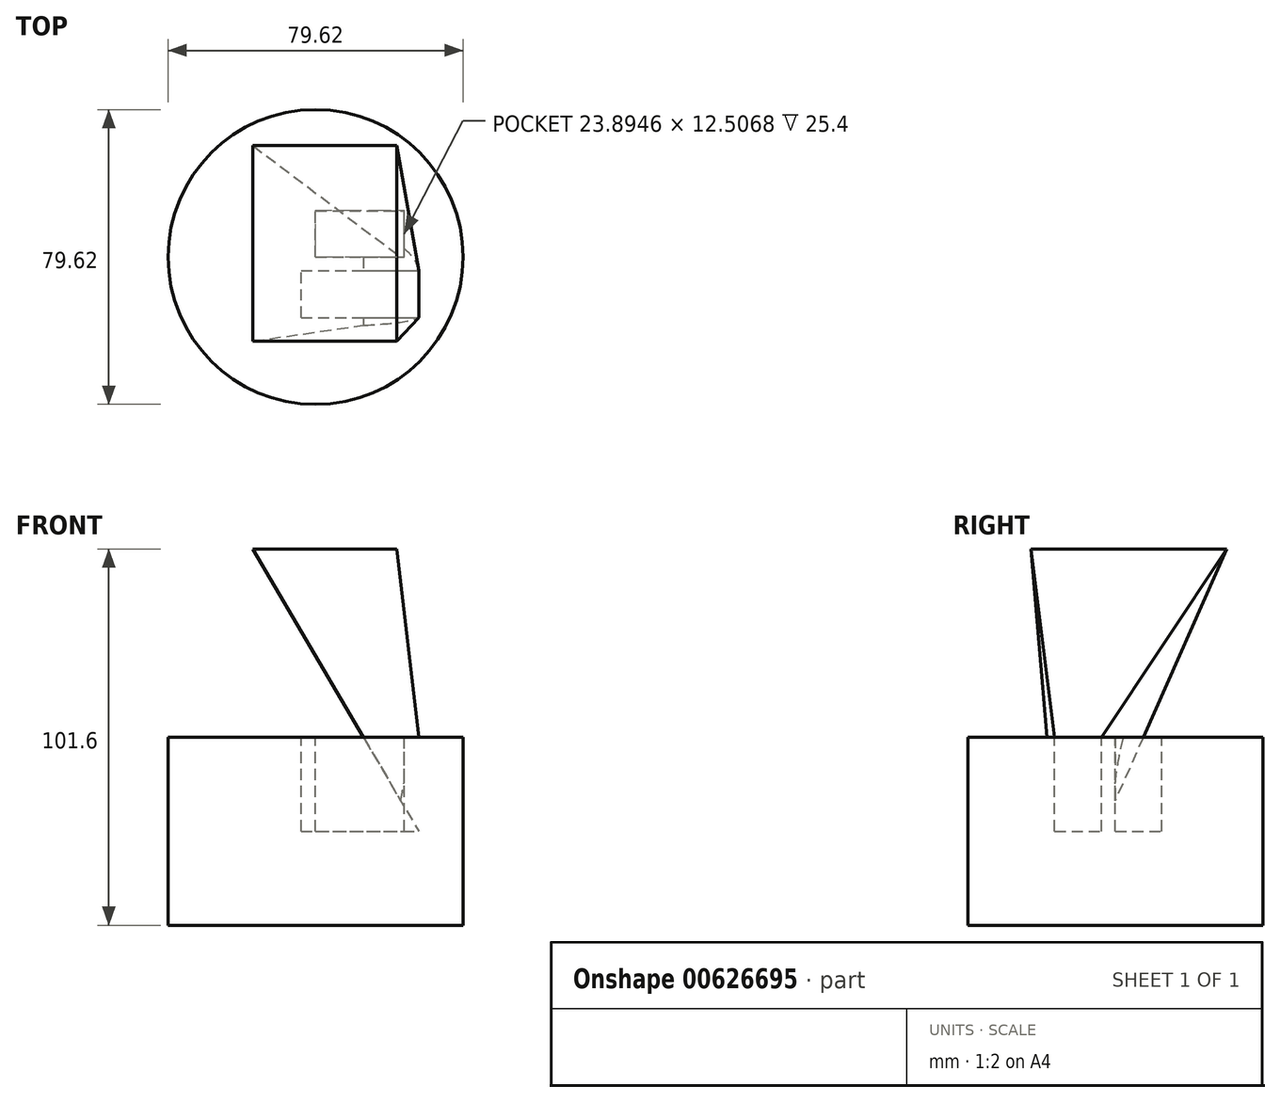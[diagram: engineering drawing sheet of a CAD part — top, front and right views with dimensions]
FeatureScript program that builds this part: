
annotation { "Feature Type Name" : "Feature", "Feature Type Description" : "" }
export const myFeature = defineFeature(function(context is Context, id is Id, definition is map)
    precondition{}
    {
        {
            var Q0;
            Q0=qCreatedBy(makeId("Top.planeOp"),FACE);
            var sketch = newSketch(context, id + "F0", { "sketchPlane" : qUnion([Q0])});
            skCircle(sketch, "E0", {"center": v(-11.95, 0) * mm, "radius": 39.8 * mm});
            skSolve(sketch);
        }
        {
            var Q0;
            Q0=makeQuery(id+"F0.imprint","IMPRINT",FACE,{"disambiguationData":[TD([[makeQuery(id+"F0.imprint","IMPRINT",EDGE,{"derivedFrom":sQuery(id+"F0.wireOp",EDGE,"E0")}),1.0]])]});
            extrude(context, id + "F1", {"entities" : qUnion([Q0]), "depth" : 25.4 * mm, "offsetDistance" : 25.4 * mm, "hasSecondDirection" : true, "secondDirectionOppositeDirection" : true, "secondDirectionDepth" : 25.4 * mm});
        }
        {
            var Q0;
            Q0=makeQuery(id+"F1.opExtrude","CAP_FACE",FACE,{"disambiguationData":[OSD([sQuery(id+"F0.wireOp",EDGE,"E0")])],"isStart":false});
            var sketch = newSketch(context, id + "F2", { "sketchPlane" : qUnion([Q0])});
            skLineSegment(sketch, "E1.bottom", {"start": v(-11.95, 0) * mm, "end": v(11.95, 0) * mm});
            skLineSegment(sketch, "E1.top", {"start": v(-11.95, 12.5) * mm, "end": v(11.95, 12.5) * mm});
            skLineSegment(sketch, "E1.left", {"start": v(-11.95, 0) * mm, "end": v(-11.95, 12.5) * mm});
            skLineSegment(sketch, "E1.right", {"start": v(11.95, 0) * mm, "end": v(11.95, 12.5) * mm});
            skPoint(sketch, "E1.middle", {"position": v(0, 6.25) * mm});
            skLineSegment(sketch, "E2.bottom", {"start": v(-15.88, -16.34) * mm, "end": v(15.88, -16.34) * mm});
            skLineSegment(sketch, "E2.top", {"start": v(-15.88, -3.64) * mm, "end": v(15.88, -3.64) * mm});
            skLineSegment(sketch, "E2.left", {"start": v(-15.88, -16.34) * mm, "end": v(-15.88, -3.64) * mm});
            skLineSegment(sketch, "E2.right", {"start": v(15.88, -16.34) * mm, "end": v(15.88, -3.64) * mm});
            skPoint(sketch, "E2.middle", {"position": v(0, -10) * mm});
            skSolve(sketch);
        }
        {
            var Q0;
            Q0=makeQuery(id+"F2.imprint","IMPRINT",FACE,{"disambiguationData":[TD([[makeQuery(id+"F2.imprint","IMPRINT",EDGE,{"derivedFrom":sQuery(id+"F2.wireOp",EDGE,"E1.bottom")}),1.0]])]});
            var Q1;
            Q1=makeQuery(id+"F2.imprint","IMPRINT",FACE,{"disambiguationData":[TD([[makeQuery(id+"F2.imprint","IMPRINT",EDGE,{"derivedFrom":sQuery(id+"F2.wireOp",EDGE,"E2.bottom")}),1.0]])]});
            var Q2;
            Q2=sQuery(id+"F2.wireOp",EDGE,"E1.left");
            var Q3;
            Q3=sQuery(id+"F2.wireOp",EDGE,"E1.top");
            var Q4;
            Q4=sQuery(id+"F2.wireOp",EDGE,"E1.right");
            var Q5;
            Q5=sQuery(id+"F2.wireOp",EDGE,"E1.bottom");
            extrude(context, id + "F3", {"entities" : qUnion([Q0, Q1]), "operationType" : NewBodyOperationType.REMOVE, "surfaceEntities" : qUnion([Q2, Q3, Q4, Q5]), "oppositeDirection" : true, "depth" : 25.4 * mm, "offsetDistance" : 25.4 * mm});
        }
        {
            var Q0;
            Q0=makeQuery(id+"F1.opExtrude","CAP_FACE",FACE,{"disambiguationData":[OSD([sQuery(id+"F0.wireOp",EDGE,"E0")])],"isStart":false});
            cPlane(context, id + "F4", {"entities" : qUnion([Q0]), "cplaneType" : CPlaneType.OFFSET, "offset" : 50.8 * mm, "width" : 152.4 * mm, "height" : 152.4 * mm});
        }
        {
            var Q0;
            Q0=qCreatedBy(id+"F4.planeOp",FACE);
            var sketch = newSketch(context, id + "F5", { "sketchPlane" : qUnion([Q0])});
            skLineSegment(sketch, "E3.bottom", {"start": v(9.94, -22.73) * mm, "end": v(-28.9, -22.73) * mm});
            skLineSegment(sketch, "E3.top", {"start": v(9.94, 30.06) * mm, "end": v(-28.9, 30.06) * mm});
            skLineSegment(sketch, "E3.left", {"start": v(9.94, -22.73) * mm, "end": v(9.94, 30.06) * mm});
            skLineSegment(sketch, "E3.right", {"start": v(-28.9, -22.73) * mm, "end": v(-28.9, 30.06) * mm});
            skPoint(sketch, "E3.middle", {"position": v(-9.48, 3.66) * mm});
            skSolve(sketch);
        }
        {
            var Q1;
            Q1=makeQuery(id+"F5.imprint","IMPRINT",FACE,{"disambiguationData":[TD([[makeQuery(id+"F5.imprint","IMPRINT",EDGE,{"derivedFrom":sQuery(id+"F5.wireOp",EDGE,"E3.bottom")}),-1.0]])]});
            var Q2;
            Q2=makeQuery(id+"F3.boolean.opBoolean","COPY",FACE,{"derivedFrom":makeQuery(id+"F3.opExtrude","SWEPT_FACE",FACE,{"disambiguationData":[OSD([sQuery(id+"F2.wireOp",EDGE,"E2.right")])]})});
            loft(context, id + "F6", {"operationType" : NewBodyOperationType.ADD, "sheetProfilesArray" : [{ "sheetProfileEntities" : qUnion([Q1]) }, { "sheetProfileEntities" : qUnion([Q2]) }]});
        }
    });
